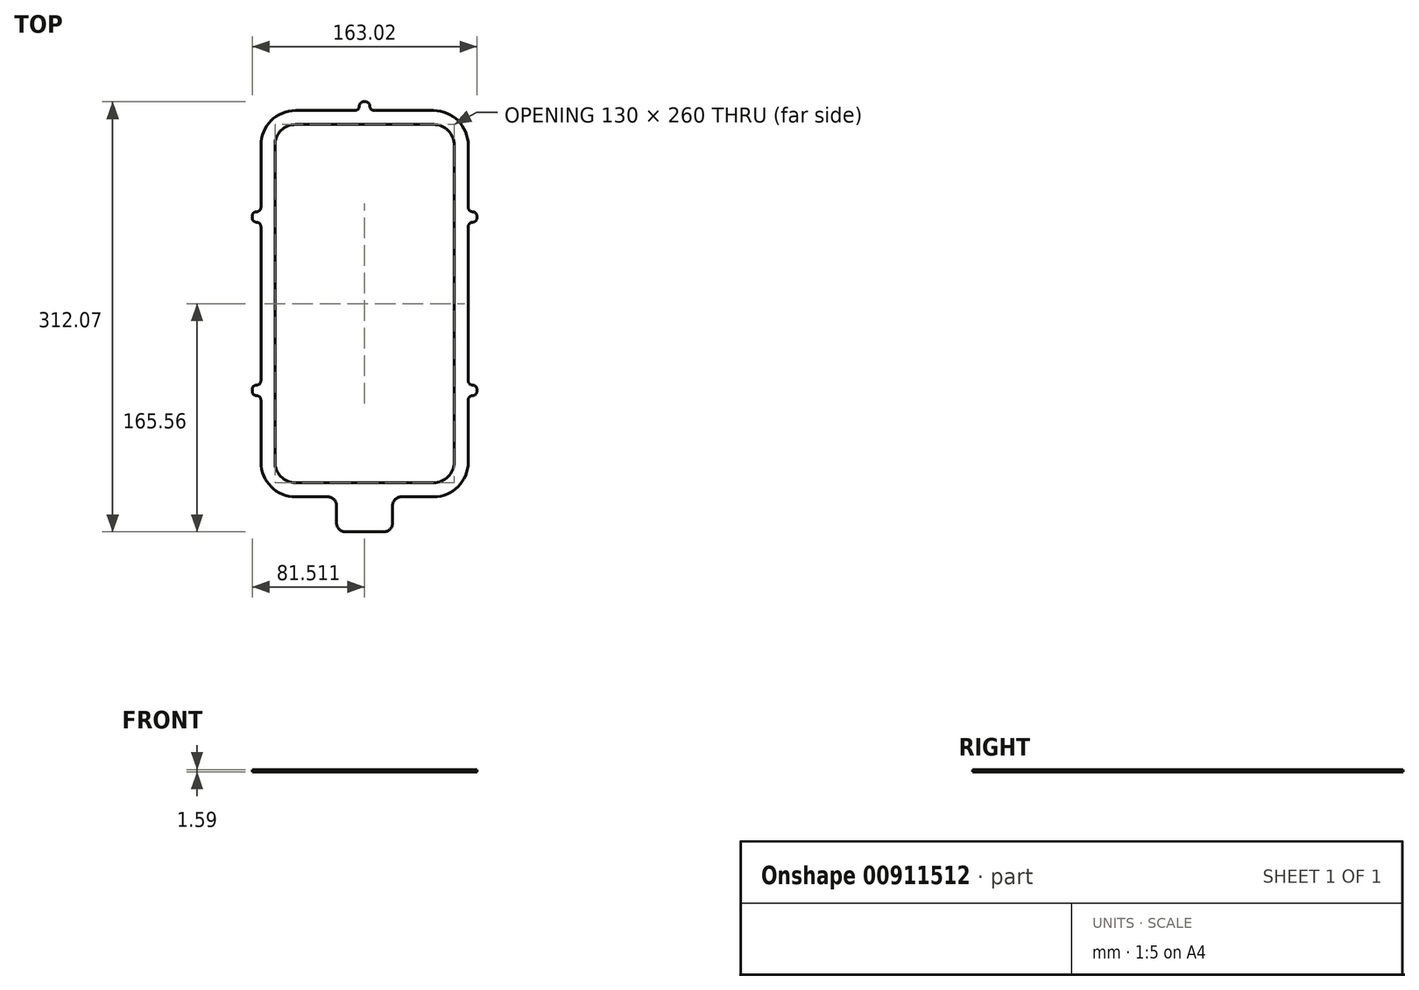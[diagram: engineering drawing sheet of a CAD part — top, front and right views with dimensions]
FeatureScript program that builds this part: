
annotation { "Feature Type Name" : "Feature", "Feature Type Description" : "" }
export const myFeature = defineFeature(function(context is Context, id is Id, definition is map)
    precondition{}
    {
        {
            var Q0;
            Q0=qCreatedBy(makeId("Top.planeOp"),FACE);
            var sketch = newSketch(context, id + "F0", { "sketchPlane" : qUnion([Q0])});
            skLineSegment(sketch, "E0.bottom", {"start": v(-50.35, -130) * mm, "end": v(49.65, -130) * mm});
            skLineSegment(sketch, "E0.top", {"start": v(-50.35, 130) * mm, "end": v(49.65, 130) * mm});
            skLineSegment(sketch, "E0.left", {"start": v(-65.35, -115) * mm, "end": v(-65.35, 115) * mm});
            skLineSegment(sketch, "E0.right", {"start": v(64.65, -115) * mm, "end": v(64.65, 115) * mm});
            skArc(sketch, "E1.filletArc", {"start": v(-50.35, 130) * mm, "mid": v(-60.96, 125.6) * mm, "end": v(-65.35, 115) * mm});
            skArc(sketch, "E2.filletArc", {"start": v(64.65, 115) * mm, "mid": v(60.26, 125.6) * mm, "end": v(49.65, 130) * mm});
            skArc(sketch, "E3.filletArc", {"start": v(-65.35, -115) * mm, "mid": v(-60.96, -125.6) * mm, "end": v(-50.35, -130) * mm});
            skArc(sketch, "E4.filletArc", {"start": v(49.65, -130) * mm, "mid": v(60.26, -125.6) * mm, "end": v(64.65, -115) * mm});
            skLineSegment(sketch, "E5.1", {"start": v(-75.5, 69.88) * mm, "end": v(-75.5, 115) * mm});
            skLineSegment(sketch, "E5.2", {"start": v(-50.35, -140.16) * mm, "end": v(-27.02, -140.16) * mm});
            skLineSegment(sketch, "E5.3", {"start": v(-50.35, 140.16) * mm, "end": v(-50.35, 140.16) * mm});
            skLineSegment(sketch, "E5.4", {"start": v(49.65, -140.16) * mm, "end": v(49.65, -140.16) * mm});
            skLineSegment(sketch, "E5.5", {"start": v(74.81, -115) * mm, "end": v(74.81, -69.88) * mm});
            skArc(sketch, "E5.6", {"start": v(74.81, 115) * mm, "mid": v(67.44, 132.8) * mm, "end": v(49.65, 140.16) * mm});
            skLineSegment(sketch, "E5.7", {"start": v(-50.35, 140.16) * mm, "end": v(-7.33, 140.16) * mm});
            skLineSegment(sketch, "E6.trimOffspring", {"start": v(74.81, 0) * mm, "end": v(74.81, 55.9) * mm});
            skPoint(sketch, "E7.visualSharp", {"position": v(74.81, 0) * mm});
            skLineSegment(sketch, "E8", {"start": v(-75.5, 0) * mm, "end": v(-75.5, -55.9) * mm});
            skLineSegment(sketch, "E9.trimOffspring", {"start": v(6.64, 140.16) * mm, "end": v(49.65, 140.16) * mm});
            skLineSegment(sketch, "E10", {"start": v(-65.35, 0) * mm, "end": v(64.65, 0) * mm, "construction": true});
            skLineSegment(sketch, "E11.trimOffspring", {"start": v(26.32, -140.16) * mm, "end": v(49.65, -140.16) * mm});
            skArc(sketch, "E12.trimOffspring", {"start": v(-50.35, 140.16) * mm, "mid": v(-68.14, 132.8) * mm, "end": v(-75.5, 115) * mm});
            skLineSegment(sketch, "E13.MirrorCS", {"start": v(74.81, 0) * mm, "end": v(-65.35, 0) * mm, "construction": true});
            skLineSegment(sketch, "E14", {"start": v(-0.35, -130) * mm, "end": v(-0.35, 130) * mm, "construction": true});
            skLineSegment(sketch, "E15.trimOffspring", {"start": v(49.65, 140.16) * mm, "end": v(49.65, 140.16) * mm});
            skArc(sketch, "E16.trimOffspring", {"start": v(49.65, -140.16) * mm, "mid": v(67.44, -132.8) * mm, "end": v(74.81, -115) * mm});
            skLineSegment(sketch, "E17.top", {"start": v(-14.32, -165.56) * mm, "end": v(13.62, -165.56) * mm});
            skLineSegment(sketch, "E17.left", {"start": v(-20.67, -146.5) * mm, "end": v(-20.67, -159.21) * mm});
            skLineSegment(sketch, "E17.right", {"start": v(19.97, -146.5) * mm, "end": v(19.97, -159.21) * mm});
            skArc(sketch, "E18", {"start": v(-75.5, -115) * mm, "mid": v(-68.14, -132.8) * mm, "end": v(-50.35, -140.16) * mm});
            skPoint(sketch, "E19.visualSharp", {"position": v(-20.67, -165.56) * mm});
            skArc(sketch, "E19.filletArc", {"start": v(-20.67, -159.21) * mm, "mid": v(-18.8, -163.7) * mm, "end": v(-14.32, -165.56) * mm});
            skPoint(sketch, "E20.visualSharp", {"position": v(19.97, -165.56) * mm});
            skArc(sketch, "E20.filletArc", {"start": v(13.62, -165.56) * mm, "mid": v(18.11, -163.7) * mm, "end": v(19.97, -159.21) * mm});
            skPoint(sketch, "E21.visualSharp", {"position": v(-20.67, -140.16) * mm});
            skPoint(sketch, "E22.newPointB", {"position": v(0, -140.16) * mm});
            skArc(sketch, "E22.filletArc", {"start": v(-20.67, -146.5) * mm, "mid": v(-22.53, -142.02) * mm, "end": v(-27.02, -140.16) * mm});
            skPoint(sketch, "E23.newPointA", {"position": v(19.97, -140.16) * mm});
            skArc(sketch, "E23.filletArc", {"start": v(26.32, -140.16) * mm, "mid": v(21.83, -142.02) * mm, "end": v(19.97, -146.5) * mm});
            skLineSegment(sketch, "E24.top", {"start": v(-0.98, 146.5) * mm, "end": v(0.29, 146.5) * mm});
            skLineSegment(sketch, "E24.left", {"start": v(-4.16, 143.34) * mm, "end": v(-4.16, 143.33) * mm});
            skLineSegment(sketch, "E24.right", {"start": v(3.46, 143.34) * mm, "end": v(3.46, 143.33) * mm});
            skPoint(sketch, "E25.visualSharp", {"position": v(-4.16, 146.5) * mm});
            skArc(sketch, "E25.filletArc", {"start": v(-0.98, 146.5) * mm, "mid": v(-3.23, 145.58) * mm, "end": v(-4.16, 143.33) * mm});
            skPoint(sketch, "E26.visualSharp", {"position": v(3.46, 146.5) * mm});
            skArc(sketch, "E26.filletArc", {"start": v(3.46, 143.33) * mm, "mid": v(2.53, 145.58) * mm, "end": v(0.29, 146.5) * mm});
            skPoint(sketch, "E27.newPointA", {"position": v(0, 140.16) * mm});
            skArc(sketch, "E27.filletArc", {"start": v(-7.33, 140.16) * mm, "mid": v(-5.09, 141.09) * mm, "end": v(-4.16, 143.34) * mm});
            skArc(sketch, "E28.filletArc", {"start": v(3.46, 143.34) * mm, "mid": v(4.4, 141.09) * mm, "end": v(6.64, 140.16) * mm});
            skLineSegment(sketch, "E29", {"start": v(-75.5, 0) * mm, "end": v(-75.5, 55.9) * mm, "construction": true});
            skLineSegment(sketch, "E30.bottom", {"start": v(-78.68, 66.7) * mm, "end": v(-78.68, 66.7) * mm});
            skLineSegment(sketch, "E30.top", {"start": v(-78.68, 59.08) * mm, "end": v(-78.68, 59.08) * mm});
            skLineSegment(sketch, "E30.right", {"start": v(-81.86, 63.53) * mm, "end": v(-81.86, 62.26) * mm});
            skPoint(sketch, "E31.visualSharp", {"position": v(-81.86, 66.7) * mm});
            skArc(sketch, "E31.filletArc", {"start": v(-78.68, 66.7) * mm, "mid": v(-80.93, 65.77) * mm, "end": v(-81.86, 63.53) * mm});
            skPoint(sketch, "E32.visualSharp", {"position": v(-81.86, 59.08) * mm});
            skArc(sketch, "E32.filletArc", {"start": v(-81.86, 62.26) * mm, "mid": v(-80.93, 60.01) * mm, "end": v(-78.68, 59.08) * mm});
            skPoint(sketch, "E33.newPointB", {"position": v(-75.5, 0) * mm});
            skArc(sketch, "E33.filletArc", {"start": v(-78.68, 66.7) * mm, "mid": v(-76.44, 67.63) * mm, "end": v(-75.5, 69.88) * mm});
            skPoint(sketch, "E34.visualSharp", {"position": v(-75.5, 59.08) * mm});
            skArc(sketch, "E34.filletArc", {"start": v(-75.5, 55.9) * mm, "mid": v(-76.44, 58.15) * mm, "end": v(-78.68, 59.08) * mm});
            skLineSegment(sketch, "E35", {"start": v(-75.5, 55.9) * mm, "end": v(-75.5, 0) * mm});
            skArc(sketch, "E36.MirrorCS", {"start": v(-78.68, -66.7) * mm, "mid": v(-80.93, -65.77) * mm, "end": v(-81.86, -63.53) * mm});
            skArc(sketch, "E37.MirrorCS", {"start": v(-78.68, -66.7) * mm, "mid": v(-76.44, -67.63) * mm, "end": v(-75.5, -69.88) * mm});
            skLineSegment(sketch, "E38.MirrorCS", {"start": v(-81.86, -63.53) * mm, "end": v(-81.86, -62.26) * mm});
            skArc(sketch, "E39.MirrorCS", {"start": v(-81.86, -62.26) * mm, "mid": v(-80.93, -60.01) * mm, "end": v(-78.68, -59.08) * mm});
            skArc(sketch, "E40.MirrorCS", {"start": v(-75.5, -55.9) * mm, "mid": v(-76.44, -58.15) * mm, "end": v(-78.68, -59.08) * mm});
            skLineSegment(sketch, "E41.trimOffspring", {"start": v(-75.5, -69.88) * mm, "end": v(-75.5, -115) * mm});
            skLineSegment(sketch, "E42.MirrorCS", {"start": v(81.16, 63.53) * mm, "end": v(81.16, 62.26) * mm});
            skPoint(sketch, "E43.MirrorP", {"position": v(81.16, 66.7) * mm});
            skArc(sketch, "E44.MirrorCS", {"start": v(81.16, 62.26) * mm, "mid": v(80.23, 60.01) * mm, "end": v(77.99, 59.08) * mm});
            skArc(sketch, "E45.MirrorCS", {"start": v(77.99, 66.7) * mm, "mid": v(75.74, 67.63) * mm, "end": v(74.81, 69.88) * mm});
            skPoint(sketch, "E46.MirrorP", {"position": v(74.81, 59.08) * mm});
            skLineSegment(sketch, "E47.MirrorCS", {"start": v(77.99, 66.7) * mm, "end": v(77.99, 66.7) * mm});
            skArc(sketch, "E48.MirrorCS", {"start": v(77.99, 66.7) * mm, "mid": v(80.23, 65.77) * mm, "end": v(81.16, 63.53) * mm});
            skArc(sketch, "E49.MirrorCS", {"start": v(74.81, 55.9) * mm, "mid": v(75.74, 58.15) * mm, "end": v(77.99, 59.08) * mm});
            skPoint(sketch, "E50.MirrorP", {"position": v(81.16, 59.08) * mm});
            skLineSegment(sketch, "E51.MirrorCS", {"start": v(77.99, 59.08) * mm, "end": v(77.99, 59.08) * mm});
            skLineSegment(sketch, "E52.MirrorCS", {"start": v(81.16, -63.53) * mm, "end": v(81.16, -62.26) * mm});
            skArc(sketch, "E53.MirrorCS", {"start": v(81.16, -62.26) * mm, "mid": v(80.23, -60.01) * mm, "end": v(77.99, -59.08) * mm});
            skArc(sketch, "E54.MirrorCS", {"start": v(77.99, -66.7) * mm, "mid": v(75.74, -67.63) * mm, "end": v(74.81, -69.88) * mm});
            skArc(sketch, "E55.MirrorCS", {"start": v(77.99, -66.7) * mm, "mid": v(80.23, -65.77) * mm, "end": v(81.16, -63.53) * mm});
            skArc(sketch, "E56.MirrorCS", {"start": v(74.81, -55.9) * mm, "mid": v(75.74, -58.15) * mm, "end": v(77.99, -59.08) * mm});
            skLineSegment(sketch, "E57.trimOffspring", {"start": v(74.81, -55.9) * mm, "end": v(74.81, 0) * mm});
            skLineSegment(sketch, "E58.trimOffspring", {"start": v(74.81, 69.88) * mm, "end": v(74.81, 115) * mm});
            skSolve(sketch);
        }
        {
            var Q0;
            Q0=makeQuery(id+"F0.imprint","IMPRINT",FACE,{"disambiguationData":[TD([[makeQuery(id+"F0.imprint","IMPRINT",EDGE,{"derivedFrom":sQuery(id+"F0.wireOp",EDGE,"E0.bottom")}),-1.0]])]});
            extrude(context, id + "F1", {"entities" : qUnion([Q0]), "depth" : 1.59 * mm, "offsetDistance" : 25.4 * mm});
        }
    });
